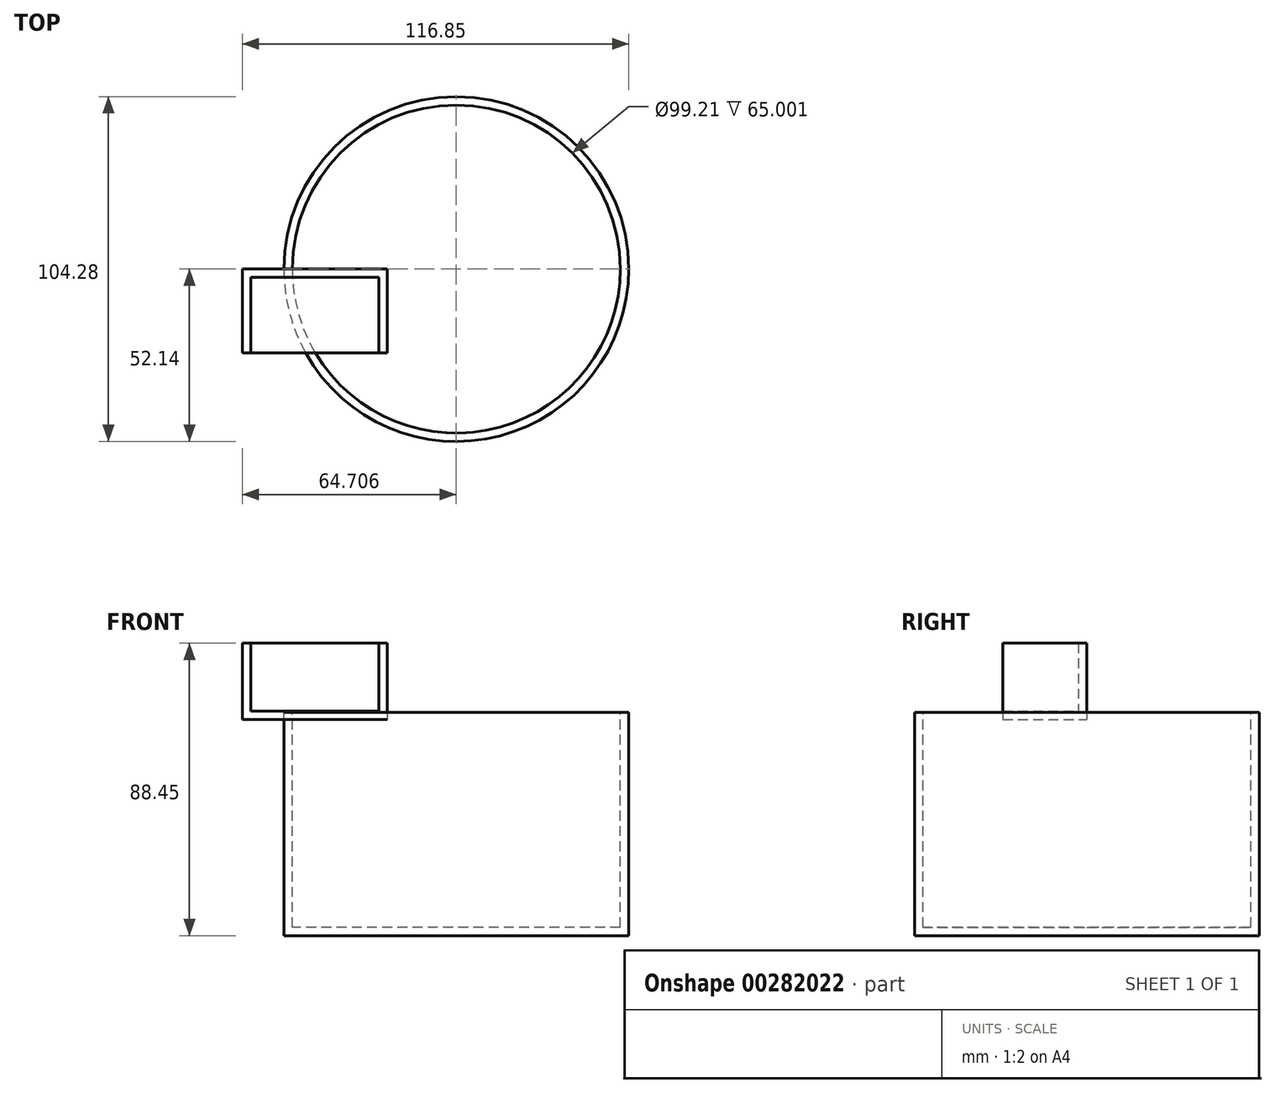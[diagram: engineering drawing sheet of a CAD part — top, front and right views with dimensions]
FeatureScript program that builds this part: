
annotation { "Feature Type Name" : "Feature", "Feature Type Description" : "" }
export const myFeature = defineFeature(function(context is Context, id is Id, definition is map)
    precondition{}
    {
        {
            var Q0;
            Q0=qCreatedBy(makeId("Front.planeOp"),FACE);
            var sketch = newSketch(context, id + "F0", { "sketchPlane" : qUnion([Q0])});
            skLineSegment(sketch, "E0.bottom", {"start": v(-61.28, 47.4) * mm, "end": v(-17.5, 47.4) * mm});
            skLineSegment(sketch, "E0.top", {"start": v(-61.28, 24.25) * mm, "end": v(-17.5, 24.25) * mm});
            skLineSegment(sketch, "E0.left", {"start": v(-61.28, 47.4) * mm, "end": v(-61.28, 24.25) * mm});
            skLineSegment(sketch, "E0.right", {"start": v(-17.5, 47.4) * mm, "end": v(-17.5, 24.25) * mm});
            skLineSegment(sketch, "E1.bottom", {"start": v(3.43, 26.5) * mm, "end": v(55.57, 26.5) * mm});
            skLineSegment(sketch, "E1.top", {"start": v(3.43, -41.05) * mm, "end": v(55.57, -41.05) * mm});
            skLineSegment(sketch, "E1.left", {"start": v(3.43, 26.5) * mm, "end": v(3.43, -41.05) * mm});
            skLineSegment(sketch, "E1.right", {"start": v(55.57, 26.5) * mm, "end": v(55.57, -41.05) * mm});
            skSolve(sketch);
        }
        {
            var Q0;
            Q0 = qSketchRegion(id + "F0", true);
            extrude(context, id + "F1", {"entities" : qUnion([Q0]), "depth" : 25.4 * mm});
        }
        {
            var Q0;
            Q0=makeQuery(id+"F1.opExtrude","SWEPT_BODY",BODY,{"disambiguationData":[OSD([sQuery(id+"F0.wireOp",EDGE,"E1.bottom"),sQuery(id+"F0.wireOp",EDGE,"E1.top"),sQuery(id+"F0.wireOp",EDGE,"E1.left"),sQuery(id+"F0.wireOp",EDGE,"E1.right")])]});
            deleteBodies(context, id + "F2", {"entities" : qUnion([Q0])});
        }
        {
            var Q0;
            Q0=makeQuery(id+"F0.imprint","IMPRINT",FACE,{"disambiguationData":[TD([[makeQuery(id+"F0.imprint","IMPRINT",EDGE,{"derivedFrom":sQuery(id+"F0.wireOp",EDGE,"E1.bottom")}),-1.0]])]});
            var Q1;
            Q1=sQuery(id+"F0.wireOp",EDGE,"E1.left");
            revolve(context, id + "F3", {"entities" : qUnion([Q0]), "axis" : qUnion([Q1]), "revolveType" : RevolveType.FULL});
        }
        {
            var Q0;
            Q0=makeQuery(id+"F1.opExtrude","SWEPT_FACE",FACE,{"disambiguationData":[OSD([sQuery(id+"F0.wireOp",EDGE,"E0.bottom")])]});
            var Q1;
            Q1=makeQuery(id+"F1.opExtrude","CAP_FACE",FACE,{"disambiguationData":[OSD([sQuery(id+"F0.wireOp",EDGE,"E0.bottom"),sQuery(id+"F0.wireOp",EDGE,"E0.top"),sQuery(id+"F0.wireOp",EDGE,"E0.left"),sQuery(id+"F0.wireOp",EDGE,"E0.right")])],"isStart":false});
            var Q2;
            Q2=makeQuery(id+"F3.opRevolve","SWEPT_FACE",FACE,{"disambiguationData":[OSD([sQuery(id+"F0.wireOp",EDGE,"E1.bottom")])]});
            shell(context, id + "F4", {"entities" : qUnion([Q0, Q1, Q2]), "thickness" : 2.54 * mm});
        }
    });
